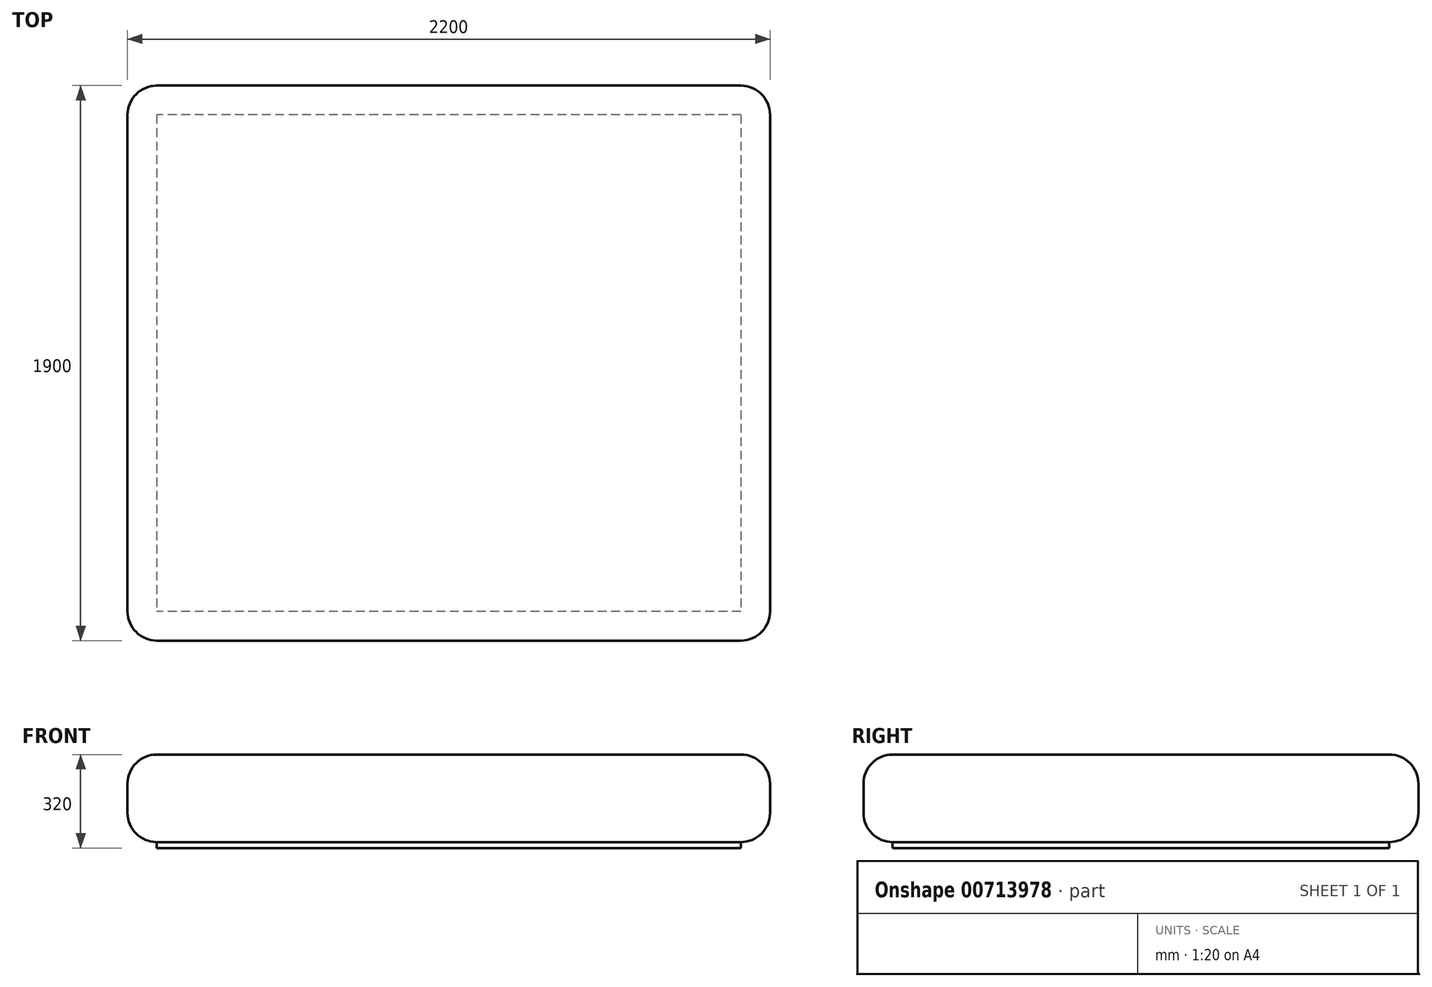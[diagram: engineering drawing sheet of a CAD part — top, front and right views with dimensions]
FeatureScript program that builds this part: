
annotation { "Feature Type Name" : "Feature", "Feature Type Description" : "" }
export const myFeature = defineFeature(function(context is Context, id is Id, definition is map)
    precondition{}
    {
        {
            var Q0;
            Q0=qCreatedBy(makeId("Top.planeOp"),FACE);
            var sketch = newSketch(context, id + "F0", { "sketchPlane" : qUnion([Q0])});
            skLineSegment(sketch, "E0.bottom", {"start": v(1000, 850) * mm, "end": v(-1000, 850) * mm});
            skLineSegment(sketch, "E0.top", {"start": v(1000, -850) * mm, "end": v(-1000, -850) * mm});
            skLineSegment(sketch, "E0.left", {"start": v(1000, 850) * mm, "end": v(1000, -850) * mm});
            skLineSegment(sketch, "E0.right", {"start": v(-1000, 850) * mm, "end": v(-1000, -850) * mm});
            skPoint(sketch, "E0.middle", {"position": v(0, 0) * mm});
            skSolve(sketch);
        }
        {
            var Q0;
            Q0=qSketchRegion(id+"F0",true);
            extrude(context, id + "F1", {"entities" : qUnion([Q0]), "depth" : 20 * mm});
        }
        {
            var Q0;
            Q0=makeQuery(id+"F1.opExtrude","CAP_FACE",FACE,{"disambiguationData":[OSD([sQuery(id+"F0.wireOp",EDGE,"E0.bottom"),sQuery(id+"F0.wireOp",EDGE,"E0.top"),sQuery(id+"F0.wireOp",EDGE,"E0.left"),sQuery(id+"F0.wireOp",EDGE,"E0.right")])],"isStart":false});
            var sketch = newSketch(context, id + "F2", { "sketchPlane" : qUnion([Q0])});
            skLineSegment(sketch, "E1.bottom", {"start": v(1100, 950) * mm, "end": v(-1100, 950) * mm});
            skLineSegment(sketch, "E1.top", {"start": v(1100, -950) * mm, "end": v(-1100, -950) * mm});
            skLineSegment(sketch, "E1.left", {"start": v(1100, 950) * mm, "end": v(1100, -950) * mm});
            skLineSegment(sketch, "E1.right", {"start": v(-1100, 950) * mm, "end": v(-1100, -950) * mm});
            skPoint(sketch, "E1.middle", {"position": v(0, 0) * mm});
            skSolve(sketch);
        }
        {
            var Q0;
            Q0=qSketchRegion(id+"F2",true);
            extrude(context, id + "F3", {"entities" : qUnion([Q0]), "depth" : 300 * mm});
        }
        {
            var Q0;
            Q0=makeQuery(id+"F3.opExtrude","CAP_FACE",FACE,{"disambiguationData":[OSD([sQuery(id+"F2.wireOp",EDGE,"E1.bottom"),sQuery(id+"F2.wireOp",EDGE,"E1.top"),sQuery(id+"F2.wireOp",EDGE,"E1.left"),sQuery(id+"F2.wireOp",EDGE,"E1.right")])],"isStart":false});
            var Q1;
            Q1=makeQuery(id+"F3.opExtrude","CAP_FACE",FACE,{"disambiguationData":[OSD([sQuery(id+"F2.wireOp",EDGE,"E1.bottom"),sQuery(id+"F2.wireOp",EDGE,"E1.top"),sQuery(id+"F2.wireOp",EDGE,"E1.left"),sQuery(id+"F2.wireOp",EDGE,"E1.right")])],"isStart":true});
            var Q2;
            Q2=makeQuery(id+"F3.opExtrude","SWEPT_EDGE",EDGE,{"disambiguationData":[OSD([sQuery(id+"F2.wireOp",EDGE,"E1.top"),sQuery(id+"F2.wireOp",EDGE,"E1.left")])]});
            var Q3;
            Q3=makeQuery(id+"F3.opExtrude","SWEPT_EDGE",EDGE,{"disambiguationData":[OSD([sQuery(id+"F2.wireOp",EDGE,"E1.bottom"),sQuery(id+"F2.wireOp",EDGE,"E1.left")])]});
            var Q4;
            Q4=makeQuery(id+"F3.opExtrude","SWEPT_EDGE",EDGE,{"disambiguationData":[OSD([sQuery(id+"F2.wireOp",EDGE,"E1.bottom"),sQuery(id+"F2.wireOp",EDGE,"E1.right")])]});
            var Q5;
            Q5=makeQuery(id+"F3.opExtrude","SWEPT_EDGE",EDGE,{"disambiguationData":[OSD([sQuery(id+"F2.wireOp",EDGE,"E1.top"),sQuery(id+"F2.wireOp",EDGE,"E1.right")])]});
            fillet(context, id + "F4", {"entities" : qUnion([Q0, Q1, Q2, Q3, Q4, Q5]), "radius" : 100 * mm, "tangentPropagation" : true, "allowEdgeOverflow" : false});
        }
    });
